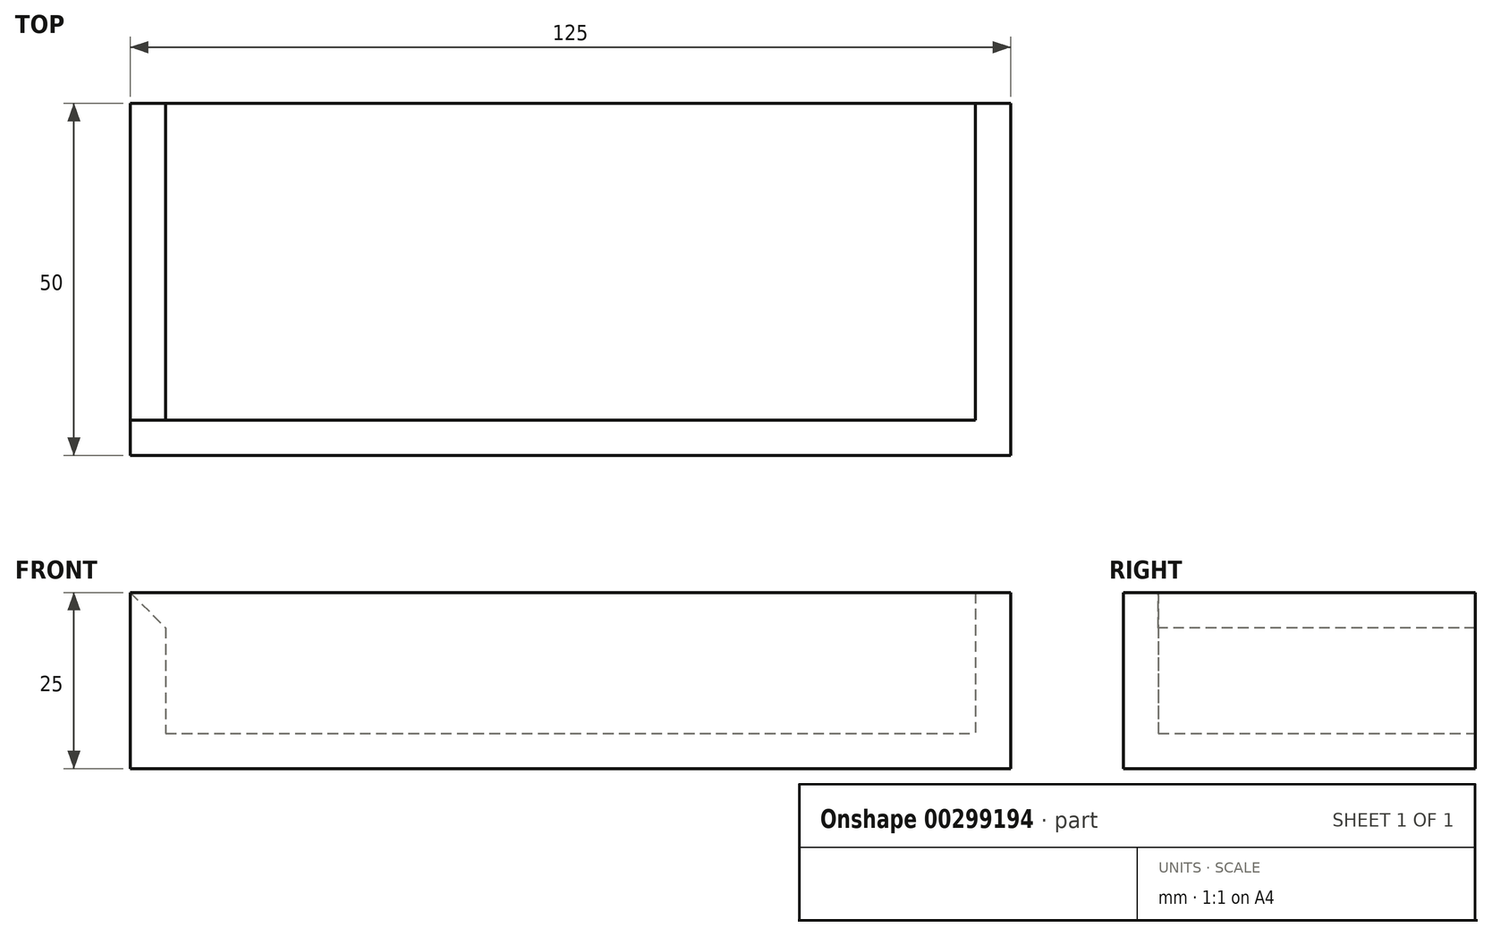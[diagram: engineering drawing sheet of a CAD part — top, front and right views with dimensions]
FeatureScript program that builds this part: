
annotation { "Feature Type Name" : "Feature", "Feature Type Description" : "" }
export const myFeature = defineFeature(function(context is Context, id is Id, definition is map)
    precondition{}
    {
        {
            var Q0;
            Q0=qCreatedBy(makeId("Top.planeOp"),FACE);
            var sketch = newSketch(context, id + "F0", { "sketchPlane" : qUnion([Q0])});
            skLineSegment(sketch, "E0.bottom", {"start": v(0, 0) * mm, "end": v(125, 0) * mm});
            skLineSegment(sketch, "E0.top", {"start": v(0, 50) * mm, "end": v(125, 50) * mm});
            skLineSegment(sketch, "E0.left", {"start": v(0, 0) * mm, "end": v(0, 50) * mm});
            skLineSegment(sketch, "E0.right", {"start": v(125, 0) * mm, "end": v(125, 50) * mm});
            skSolve(sketch);
        }
        {
            var Q0;
            Q0 = qSketchRegion(id + "F0", true);
            extrude(context, id + "F1", {"entities" : qUnion([Q0]), "depth" : 25 * mm});
        }
        {
            var Q0;
            Q0=makeQuery(id+"F1.opExtrude","CAP_FACE",FACE,{"disambiguationData":[OSD([sQuery(id+"F0.wireOp",EDGE,"E0.bottom"),sQuery(id+"F0.wireOp",EDGE,"E0.top"),sQuery(id+"F0.wireOp",EDGE,"E0.left"),sQuery(id+"F0.wireOp",EDGE,"E0.right")])],"isStart":false});
            var Q1;
            Q1=makeQuery(id+"F1.opExtrude","SWEPT_FACE",FACE,{"disambiguationData":[OSD([sQuery(id+"F0.wireOp",EDGE,"E0.top")])]});
            shell(context, id + "F2", {"entities" : qUnion([Q0, Q1]), "thickness" : 5 * mm});
        }
        {
            var Q0;
            {var subQ0=sQuery(id+"F0.wireOp",EDGE,"E0.left");Q0=makeQuery(id+"F2.opShell","OFFSET_EDGE",EDGE,{"disambiguationData":[OSD([subQ0]),TDD([makeQuery(id+"F1.opExtrude","CAP_EDGE",EDGE,{"disambiguationData":[OSD([subQ0])],"isStart":false})])]});}
            chamfer(context, id + "F3", {"entities" : qUnion([Q0]), "width" : 5 * mm, "tangentPropagation" : true});
        }
    });
